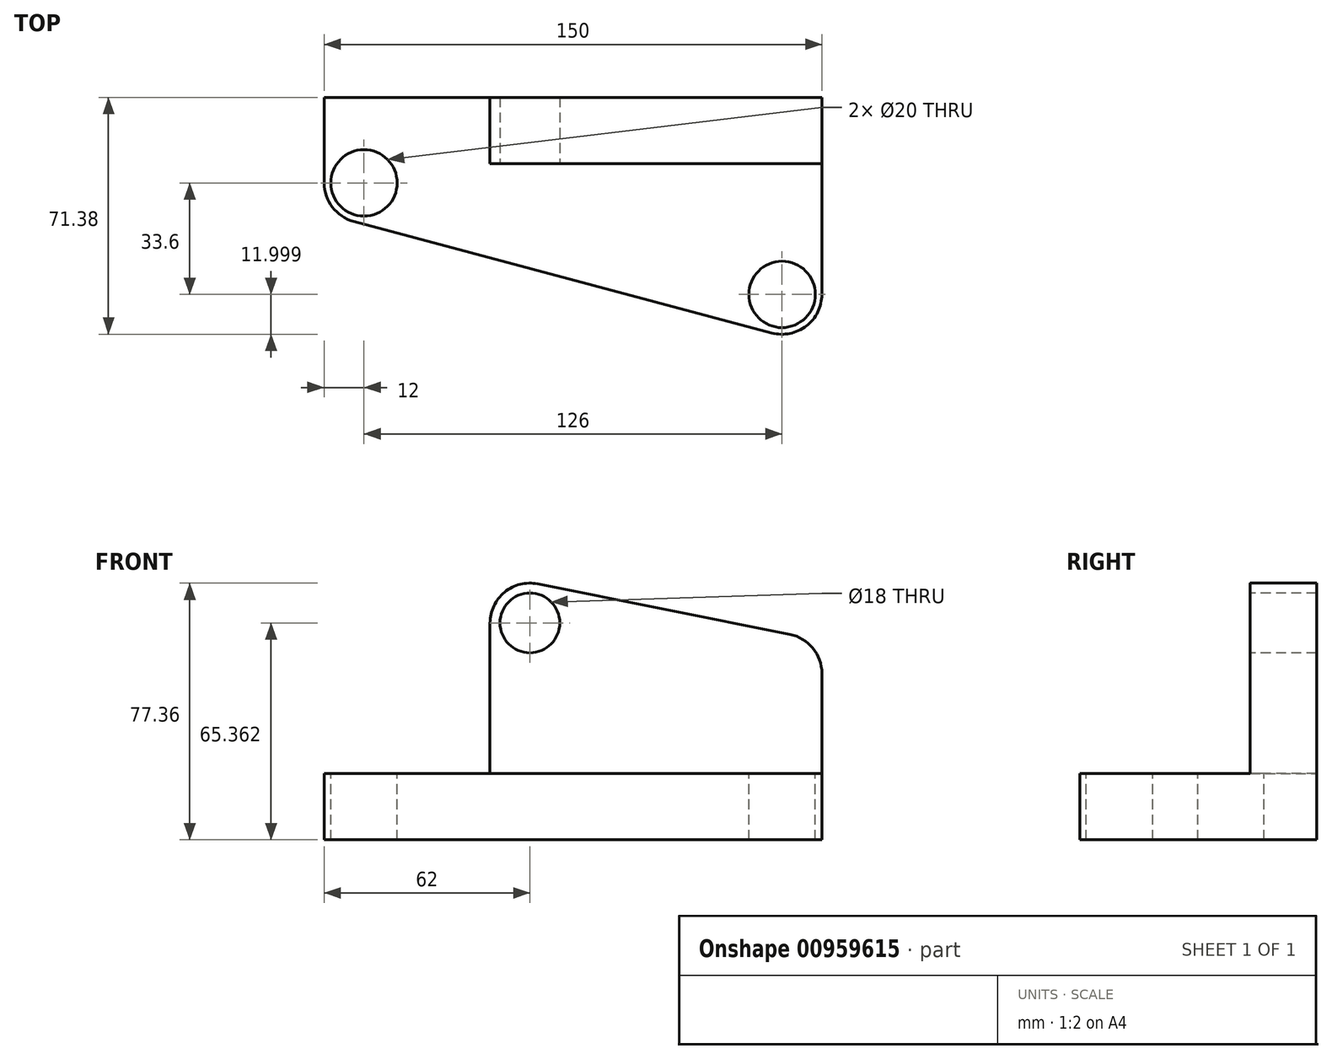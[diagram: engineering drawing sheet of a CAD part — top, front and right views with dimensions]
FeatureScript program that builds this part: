
annotation { "Feature Type Name" : "Feature", "Feature Type Description" : "" }
export const myFeature = defineFeature(function(context is Context, id is Id, definition is map)
    precondition{}
    {
        {
            var Q0;
            Q0=qCreatedBy(makeId("Top.planeOp"),FACE);
            var sketch = newSketch(context, id + "F0", { "sketchPlane" : qUnion([Q0])});
            skLineSegment(sketch, "E0", {"start": v(0, 0) * mm, "end": v(150, 0) * mm});
            skLineSegment(sketch, "E1", {"start": v(0, 0) * mm, "end": v(0, -35) * mm});
            skLineSegment(sketch, "E2", {"start": v(150, 0) * mm, "end": v(150, -75) * mm});
            skLineSegment(sketch, "E3", {"start": v(0, -35) * mm, "end": v(150, -75) * mm});
            skSolve(sketch);
        }
        {
            var Q0;
            Q0=makeQuery(id+"F0.imprint","IMPRINT",FACE,{"disambiguationData":[TD([[makeQuery(id+"F0.imprint","IMPRINT",EDGE,{"derivedFrom":sQuery(id+"F0.wireOp",EDGE,"E0")}),-1.0]])]});
            extrude(context, id + "F1", {"entities" : qUnion([Q0]), "depth" : -20 * mm, "offsetDistance" : 25 * mm});
        }
        {
            var Q0;
            Q0=makeQuery(id+"F1.opExtrude","SWEPT_FACE",FACE,{"disambiguationData":[OSD([sQuery(id+"F0.wireOp",EDGE,"E0")])]});
            var sketch = newSketch(context, id + "F2", { "sketchPlane" : qUnion([Q0])});
            skLineSegment(sketch, "E4", {"start": v(-150, -20) * mm, "end": v(-150, 40) * mm});
            skLineSegment(sketch, "E5", {"start": v(-150, 40) * mm, "end": v(-50, 60) * mm});
            skLineSegment(sketch, "E6", {"start": v(-50, 60) * mm, "end": v(-50, -20) * mm});
            skSolve(sketch);
        }
        {
            var Q0;
            {var subQ3=sQuery(id+"F2.wireOp",EDGE,"E5");Q0=makeQuery(id+"F2.imprint","IMPRINT",FACE,{"disambiguationData":[TD([[makeQuery(id+"F2.imprint","IMPRINT",EDGE,{"derivedFrom":subQ3}),-1.0]])]});}
            extrude(context, id + "F3", {"entities" : qUnion([Q0]), "operationType" : NewBodyOperationType.ADD, "depth" : -20 * mm, "offsetDistance" : 25 * mm});
        }
        {
            var Q0;
            Q0=makeQuery(id+"F1.opExtrude","SWEPT_EDGE",EDGE,{"disambiguationData":[OSD([sQuery(id+"F0.wireOp",EDGE,"E1"),sQuery(id+"F0.wireOp",EDGE,"E3")])]});
            var Q1;
            Q1=makeQuery(id+"F1.opExtrude","SWEPT_EDGE",EDGE,{"disambiguationData":[OSD([sQuery(id+"F0.wireOp",EDGE,"E2"),sQuery(id+"F0.wireOp",EDGE,"E3")])]});
            var Q2;
            Q2=makeQuery(id+"F3.opExtrude","SWEPT_EDGE",EDGE,{"disambiguationData":[OSD([sQuery(id+"F2.wireOp",EDGE,"E5"),sQuery(id+"F2.wireOp",EDGE,"E6")])]});
            var Q3;
            Q3=makeQuery(id+"F3.opExtrude","SWEPT_EDGE",EDGE,{"disambiguationData":[OSD([sQuery(id+"F2.wireOp",EDGE,"E4"),sQuery(id+"F2.wireOp",EDGE,"E5")])]});
            fillet(context, id + "F4", {"entities" : qUnion([Q0, Q1, Q2, Q3]), "radius" : 12 * mm, "tangentPropagation" : true, "allowEdgeOverflow" : false});
        }
        {
            var Q0;
            Q0=makeQuery(id+"F1.opExtrude","CAP_FACE",FACE,{"disambiguationData":[OSD([sQuery(id+"F0.wireOp",EDGE,"E0"),sQuery(id+"F0.wireOp",EDGE,"E1"),sQuery(id+"F0.wireOp",EDGE,"E2"),sQuery(id+"F0.wireOp",EDGE,"E3")])],"isStart":true});
            var sketch = newSketch(context, id + "F5", { "sketchPlane" : qUnion([Q0])});
            skCircle(sketch, "E7", {"center": v(12, -25.78) * mm, "radius": 10 * mm});
            skSolve(sketch);
        }
        {
            var Q0;
            Q0 = qSketchRegion(id + "F5", true);
            extrude(context, id + "F6", {"entities" : qUnion([Q0]), "operationType" : NewBodyOperationType.REMOVE, "oppositeDirection" : true, "depth" : 25 * mm, "offsetDistance" : 25 * mm});
        }
        {
            var Q0;
            Q0=makeQuery(id+"F1.opExtrude","CAP_FACE",FACE,{"disambiguationData":[OSD([sQuery(id+"F0.wireOp",EDGE,"E0"),sQuery(id+"F0.wireOp",EDGE,"E1"),sQuery(id+"F0.wireOp",EDGE,"E2"),sQuery(id+"F0.wireOp",EDGE,"E3")])],"isStart":true});
            var sketch = newSketch(context, id + "F7", { "sketchPlane" : qUnion([Q0])});
            skCircle(sketch, "E8", {"center": v(138, -59.38) * mm, "radius": 10 * mm});
            skSolve(sketch);
        }
        {
            var Q0;
            Q0=makeQuery(id+"F7.imprint","IMPRINT",FACE,{"disambiguationData":[TD([[makeQuery(id+"F7.imprint","IMPRINT",EDGE,{"derivedFrom":sQuery(id+"F7.wireOp",EDGE,"E8")}),1.0]])]});
            extrude(context, id + "F8", {"entities" : qUnion([Q0]), "operationType" : NewBodyOperationType.REMOVE, "oppositeDirection" : true, "depth" : 25 * mm, "offsetDistance" : 25 * mm});
        }
        {
            var Q0;
            Q0=makeQuery(id+"F3.opExtrude","CAP_FACE",FACE,{"disambiguationData":[OSD([sQuery(id+"F0.wireOp",EDGE,"E0"),sQuery(id+"F2.wireOp",EDGE,"E4"),sQuery(id+"F2.wireOp",EDGE,"E5"),sQuery(id+"F2.wireOp",EDGE,"E6")])],"isStart":false});
            var sketch = newSketch(context, id + "F9", { "sketchPlane" : qUnion([Q0])});
            skCircle(sketch, "E9", {"center": v(62, 45.36) * mm, "radius": 9 * mm});
            skSolve(sketch);
        }
        {
            var Q0;
            Q0=makeQuery(id+"F9.imprint","IMPRINT",FACE,{"disambiguationData":[TD([[makeQuery(id+"F9.imprint","IMPRINT",EDGE,{"derivedFrom":sQuery(id+"F9.wireOp",EDGE,"E9")}),1.0]])]});
            var Q1;
            Q1=sQuery(id+"F9.wireOp",EDGE,"E9");
            extrude(context, id + "F10", {"entities" : qUnion([Q0]), "operationType" : NewBodyOperationType.REMOVE, "surfaceEntities" : qUnion([Q1]), "oppositeDirection" : true, "depth" : 25 * mm, "offsetDistance" : 25 * mm});
        }
    });
